# Revit family: 210_HRU-MinistAir-W-450
name_source: partatom
category: Mechanical Equipment
units: mm (PartAtom-declared; Revit-internal decimal feet)

## family parameters
Always vertical = Yes
Cut with Voids When Loaded = No
Part Type = Breaks Into
Room Calculation Point = No
Round Connector Dimension = Use Diameter
Shared = No
Work Plane-Based = No

## types (1)
- HRU-MinistAir-W-450
    D = 160 mm
    Description = HEAT AND ENERGY RECOVERY VENTILATORS
    H = 725 mm  [stored 2.37861 ft]
    H1 = 72 mm  [stored 0.23622 ft]
    L1 = 71 mm  [stored 0.23294 ft]
    LL = 355 mm  [stored 1.1647 ft]
    LX = 284 mm  [stored 0.931759 ft]
    MC Product Code = HRU-MinistAir-W-450
    Manufacturer = Alnor
    QmdConnectorList = 221;D;231;D;241;D;251;D
    URL = http://www.ventilation-alnor.co.uk
    W = 500 mm  [stored 1.64042 ft]
    W1 = 153 mm
    WW = 305 mm  [stored 1.00066 ft]
    X1 = 250 mm  [stored 0.82021 ft]
    Y1 = 100 mm  [stored 0.328084 ft]
    Y2 = 180 mm  [stored 0.590551 ft]
    magiPartTypeId = 210
    magiProductFamilyId = HRU-MinistAir-W-450
    magiProductId = HRU-MinistAir-W-450

note: [stored X ft] marks values corroborated as IEEE doubles in the binary element streams (Revit-internal decimal feet)

## geometry (parser evidence)
native form markers: Blend x4, Sweep x3
no freeform markers — native parametric forms only
